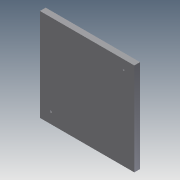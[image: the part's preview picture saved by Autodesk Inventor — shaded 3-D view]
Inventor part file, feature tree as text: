
AUTODESK INVENTOR PART (.ipt)
format: ipt  version: 2011 (Build 150239000, 239)  size: 219,136 bytes
history: native  units: in
note: dims shown in document units (in); Inventor stores cm internally (conversion verified against a paired STEP export)
features: extrude x18, sketch x18
ambient origin geometry x8: Origin, YZ Plane, XZ Plane, XY Plane, X Axis, Y Axis, Z Axis, Center Point
bodies: Solid1 (feature_tree)
feature tree (36):
  extrude  "Extrusion1"  Depth=1.9685in
  extrude  "Extrusion2"  Depth=0.375in TaperAngle=0.0deg
  extrude  "Extrusion3"  Depth=0.5906in
  extrude  "Extrusion4"  Depth=0.5906in
  extrude  "Extrusion5"  Depth=0.7874in
  extrude  "Extrusion6"  Depth=0.7874in
  extrude  "Extrusion7"  Depth=0.0394in
  extrude  "Extrusion8"  Depth=1.0in TaperAngle=0.0deg
  extrude  "Extrusion9"  Depth=0.0625in
  extrude  "Extrusion10"  Depth=0.125in TaperAngle=0.0deg
  extrude  "Extrusion11"  Depth=0.05in TaperAngle=0.0deg
  extrude  "Extrusion12"  Depth=0.05in TaperAngle=0.0deg
  extrude  "Extrusion13"  Depth=0.05in TaperAngle=0.0deg
  extrude  "Extrusion14"  Depth=0.0394in TaperAngle=0.0deg
  extrude  "Extrusion15"  Depth=0.0394in TaperAngle=0.0deg
  extrude  "Extrusion16"  Depth=0.0787in TaperAngle=0.0deg
  extrude  "Extrusion17"  [1 undecoded]
  extrude  "Extrusion18"  [1 undecoded]
  sketch  "Sketch1"  dims[d0=1.9685in d1=1.9685in]
  sketch  "Sketch2"  dims[d2=0.125in d3=0.0in d4=0.375in d5=0.0in]
  sketch  "Sketch3"  dims[d6=0.125in d7=0.5906in]
  sketch  "Sketch4"  dims[d8=0.125in d9=0.5906in]
  sketch  "Sketch5"  dims[d10=0.375in d11=0.0in d12=0.7874in]
  sketch  "Sketch6"  dims[d13=0.1969in d14=0.7874in]
  sketch  "Sketch7"  dims[d15=0.1969in d16=0.0394in]
  sketch  "Sketch8"  dims[d17=0.0394in d18=1.0in d19=0.0in]
  sketch  "Sketch9"  dims[d20=0.0625in d21=0.0625in]
  sketch  "Sketch10"  dims[d22=1.0in d23=0.0in d24=0.125in d25=0.0in]
  sketch  "Sketch11"  dims[d26=0.05in d27=0.0in d28=0.05in d29=0.0in]
  sketch  "Sketch12"  dims[d30=0.125in d31=0.0in d32=0.05in d33=0.0in]
  sketch  "Sketch13"  dims[d34=0.05in d35=0.0in d36=0.05in d37=0.0in]
  sketch  "Sketch14"  dims[d38=0.05in d39=0.0in d40=0.0394in d41=0.0in]
  sketch  "Sketch15"  dims[d42=0.0394in d43=0.0in d44=0.0394in d45=0.0in]
  sketch  "Sketch16"  dims[d46=0.0787in d47=0.0in d48=0.0787in d49=0.0in]
  sketch  "Sketch17"
  sketch  "Sketch18"
note: 2 required parameter values undecoded (feature->parameter linkage not recoverable at this tier; creation-order binding heuristic only, values carry confidence <= 0.55)
